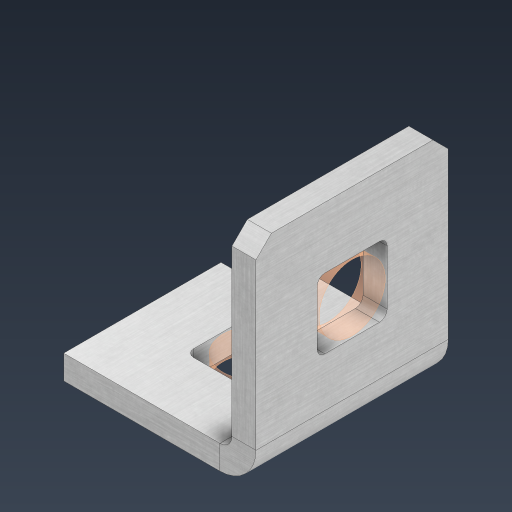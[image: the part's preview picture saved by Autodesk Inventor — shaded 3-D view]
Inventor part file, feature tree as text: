
AUTODESK INVENTOR PART (.ipt)
format: ipt  version: 2024.3 (Build 283343000, 343)  size: 411,648 bytes
history: native  units: in
note: dims shown in document units (in); Inventor stores cm internally (conversion verified against a paired STEP export)
features: other x12, sheet_metal_op x11, extrude x3, pattern_linear x2, mirror x1, chamfer x1, sketch x1
ambient origin geometry x8: Origin, YZ Plane, XZ Plane, XY Plane, X Axis, Y Axis, Z Axis, Center Point
bodies: Solid1 (feature_tree), Body (feature_tree)
feature tree (31):
  sheet_metal_op  "Flanges"
  other  "Flange Pattern Plane"
  other  "Flange Pattern Sketch"
  sheet_metal_op  "Flange Pattern"
  sheet_metal_op  "Body Pattern"
  pattern_linear  "Center Pattern"  Spacing1=0.5in  [1 undecoded]
  other  "Arc Length"
  mirror  "Notch Mirror"
  pattern_linear  "Notch Pattern"  Spacing1=0.0625in  [1 undecoded]
  chamfer  "End Chamfer"
  extrude  "Half Cut"  Depth=0.0625in
  other  "Plate1"
  sketch  "Sketch2"  dims[d0=1.0in d1=0.5in d2=0.0625in d3=0.0625in d4=0.0312in d5=0.125in d6=0.0625in d7=0.5in d8=90.0deg d9=0.0312in d10=0.25in d11=0.0625in d12=0.0625in d16=0.182in d17=0.02in d18=0.0625in d19=0.0in d20=0.25in d21=0.25in d38=0.3937in d40=0.5in d41=0.3937in d43=1.0in d46=0.172in d47=1.0in d48=0.0in d49=0.182in d50=0.02in d51=0.25in d52=0.25in d53=0.0625in d54=0.0in d55=0.172in d56=1.0in d57=0.0in d58=0.25in d60=0.3937in d62=0.5in d63=0.3937in d65=0.5in d85=0.1473in d86=0.1782in d88=0.04in d89=0.0625in d90=0.0in d91=0.04in d92=0.0491in d95=2.5in d96=0.04in d97=0.25in d98=45.0deg d99=0.25in d100=0.5in d101=0.0in d102=2.497in d106=0.182in d107=0.02in d108=0.5in d109=0.5in d110=0.0625in d111=0.0in d112=0.172in d113=0.5in d114=0.0in d117=0.5in d118=0.5in d119=0.5in]
  other  "Plate2"
  sheet_metal_op  "Bend1"
  sheet_metal_op  "Corner1"
  other  "Srf1"
  other  "Srf2"
  other  "Srf91"
  sheet_metal_op  "Body Pattern Sketch"
  other  "Srf92"
  other  "Srf786"
  sheet_metal_op  "Flange Stamp"
  sheet_metal_op  "Flange Circle"
  sheet_metal_op  "Body Stamp"
  sheet_metal_op  "Body Circle"
  other  "Center Stamp"
  other  "Center Circle"
  sheet_metal_op  "Notch"
  extrude  "ExtrusionSrf2"  Depth=0.0312in
  extrude  "ExtrusionSrf92"  Depth=0.5in
note: 2 required parameter values undecoded (feature->parameter linkage not recoverable at this tier; creation-order binding heuristic only, values carry confidence <= 0.55)
